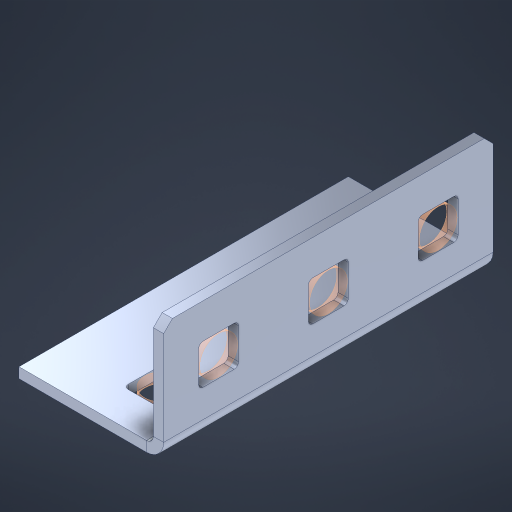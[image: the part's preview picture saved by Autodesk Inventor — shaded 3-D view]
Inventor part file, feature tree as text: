
AUTODESK INVENTOR PART (.ipt)
format: ipt  version: 2023 (Build 270158000, 158)  size: 401,920 bytes
history: native  units: in
note: dims shown in document units (in); Inventor stores cm internally (conversion verified against a paired STEP export)
features: other x11, sheet_metal_op x10, sketch x8, extrude x5, mirror x1, pattern_linear x1, chamfer x1
ambient origin geometry x8: Origin, YZ Plane, XZ Plane, XY Plane, X Axis, Y Axis, Z Axis, Center Point
bodies: Solid1 (feature_tree), Body (feature_tree)
feature tree (37):
  other  "Flange Pattern Plane"
  sheet_metal_op  "Flange Pattern"
  sheet_metal_op  "Body Pattern"
  other  "Arc Length"
  mirror  "Notch Mirror"
  pattern_linear  "Notch Pattern"  Spacing1=0.1875in  [1 undecoded]
  chamfer  "End Chamfer"
  extrude  "Half Cut"  Depth=0.0469in
  sketch  "Sketch1"  dims[d0=2.5in]
  other  "Plate1"
  sketch  "Sketch2"  dims[d1=1.5in]
  other  "Plate2"
  sheet_metal_op  "Bend1"
  sheet_metal_op  "Corner1"
  sketch  "Sketch3"  dims[d2=0.0469in]
  other  "Flange Pattern Sketch"
  sketch  "Sketch7"  dims[d3=0.0469in]
  other  "Srf1"
  other  "Srf2"
  sketch  "Sketch8"  dims[d4=0.0234in]
  sketch  "Sketch9"  dims[d5=0.0938in]
  other  "Srf91"
  sheet_metal_op  "Body Pattern Sketch"
  other  "Srf92"
  sketch  "Sketch13"  dims[d6=0.0469in]
  sketch  "Sketch14"  dims[d7=0.5in d8=90.0deg d9=0.0312in d10=0.1875in d11=0.0469in d12=0.0469in d16=0.182in d17=0.02in d18=0.0469in d19=0.0in d20=0.25in d21=0.25in d46=0.172in d47=1.0in d48=0.0in d49=0.182in d50=0.02in d51=0.25in d52=0.25in d53=0.0469in d54=0.0in d55=0.172in d56=1.0in d57=0.0in d60=1.1811in d62=0.5in d63=0.3937in d65=0.5in d85=0.1227in d86=0.1659in d88=0.04in d89=0.0469in d90=0.0in d91=0.04in d92=0.0491in d95=2.5in d96=0.04in d97=0.25in d98=45.0deg d101=0.0in d102=2.497in d131=0.5in d132=1.1811in d134=0.5in d139=0.5in]
  other  "Srf856"
  other  "Srf1310"
  sheet_metal_op  "Flange Stamp"
  sheet_metal_op  "Flange Circle"
  sheet_metal_op  "Body Stamp"
  sheet_metal_op  "Body Circle"
  sheet_metal_op  "Notch"
  extrude  "ExtrusionSrf2"  Depth=0.0469in
  extrude  "ExtrusionSrf92"  Depth=0.182in
  extrude  "ExtrusionSrf856"  Depth=0.02in
  extrude  "ExtrusionSrf1310"  Depth=0.0469in
note: 1 required parameter value undecoded (feature->parameter linkage not recoverable at this tier; creation-order binding heuristic only, values carry confidence <= 0.55)
